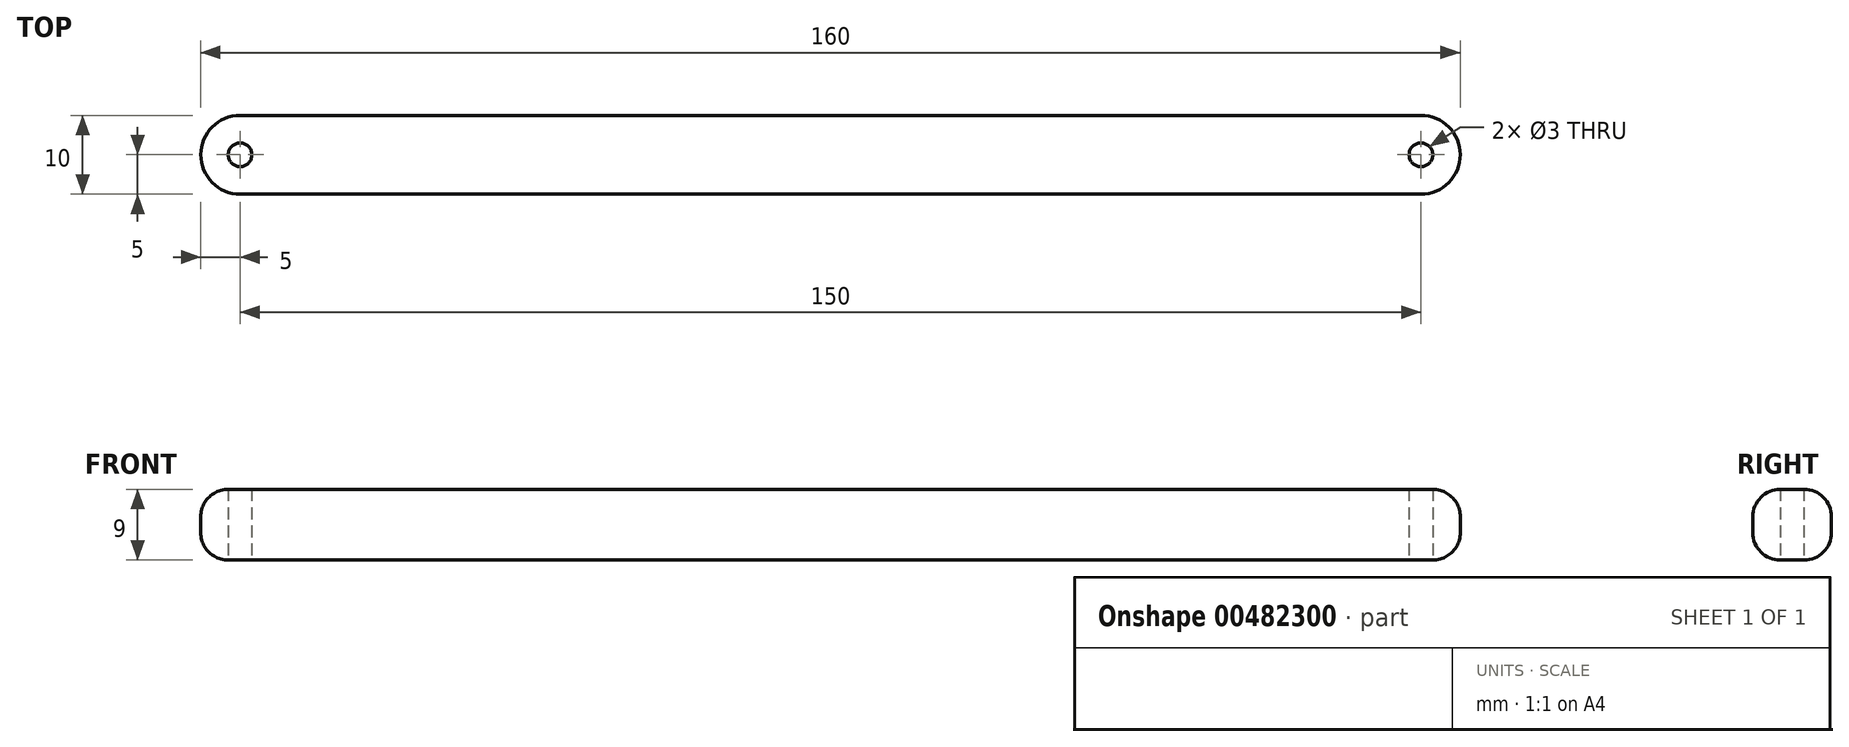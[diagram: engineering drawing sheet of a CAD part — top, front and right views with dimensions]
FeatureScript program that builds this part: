
annotation { "Feature Type Name" : "Feature", "Feature Type Description" : "" }
export const myFeature = defineFeature(function(context is Context, id is Id, definition is map)
    precondition{}
    {
        {
            var Q0;
            Q0=qCreatedBy(makeId("Top.planeOp"),FACE);
            var sketch = newSketch(context, id + "F0", { "sketchPlane" : qUnion([Q0])});
            skLineSegment(sketch, "E0", {"start": v(0, 0) * mm, "end": v(150, 0) * mm, "construction": true});
            skCircle(sketch, "E1", {"center": v(150, 0) * mm, "radius": 1.5 * mm});
            skCircle(sketch, "E2", {"center": v(0, 0) * mm, "radius": 1.5 * mm});
            skArc(sketch, "E3", {"start": v(0, 5) * mm, "mid": v(-5, 0) * mm, "end": v(0, -5) * mm});
            skLineSegment(sketch, "E4", {"start": v(0, 0) * mm, "end": v(0, 1.5) * mm, "construction": true});
            skArc(sketch, "E5", {"start": v(150, -5) * mm, "mid": v(155, 0) * mm, "end": v(150, 5) * mm});
            skLineSegment(sketch, "E6", {"start": v(0, -5) * mm, "end": v(150, -5) * mm});
            skLineSegment(sketch, "E7", {"start": v(0, 5) * mm, "end": v(150, 5) * mm});
            skSolve(sketch);
        }
        {
            var Q0;
            Q0=makeQuery(id+"F0.imprint","IMPRINT",FACE,{"disambiguationData":[TD([[makeQuery(id+"F0.imprint","IMPRINT",EDGE,{"derivedFrom":sQuery(id+"F0.wireOp",EDGE,"E1")}),-1.0]])]});
            extrude(context, id + "F1", {"entities" : qUnion([Q0]), "depth" : 9 * mm});
        }
        {
            var Q0;
            Q0=makeQuery(id+"F1.opExtrude","CAP_EDGE",EDGE,{"disambiguationData":[OSD([sQuery(id+"F0.wireOp",EDGE,"E7")])],"isStart":false});
            var Q1;
            Q1=makeQuery(id+"F1.opExtrude","CAP_EDGE",EDGE,{"disambiguationData":[OSD([sQuery(id+"F0.wireOp",EDGE,"E6")])],"isStart":true});
            fillet(context, id + "F2", {"entities" : qUnion([Q0, Q1]), "radius" : 3.5 * mm, "tangentPropagation" : true, "allowEdgeOverflow" : false});
        }
    });
